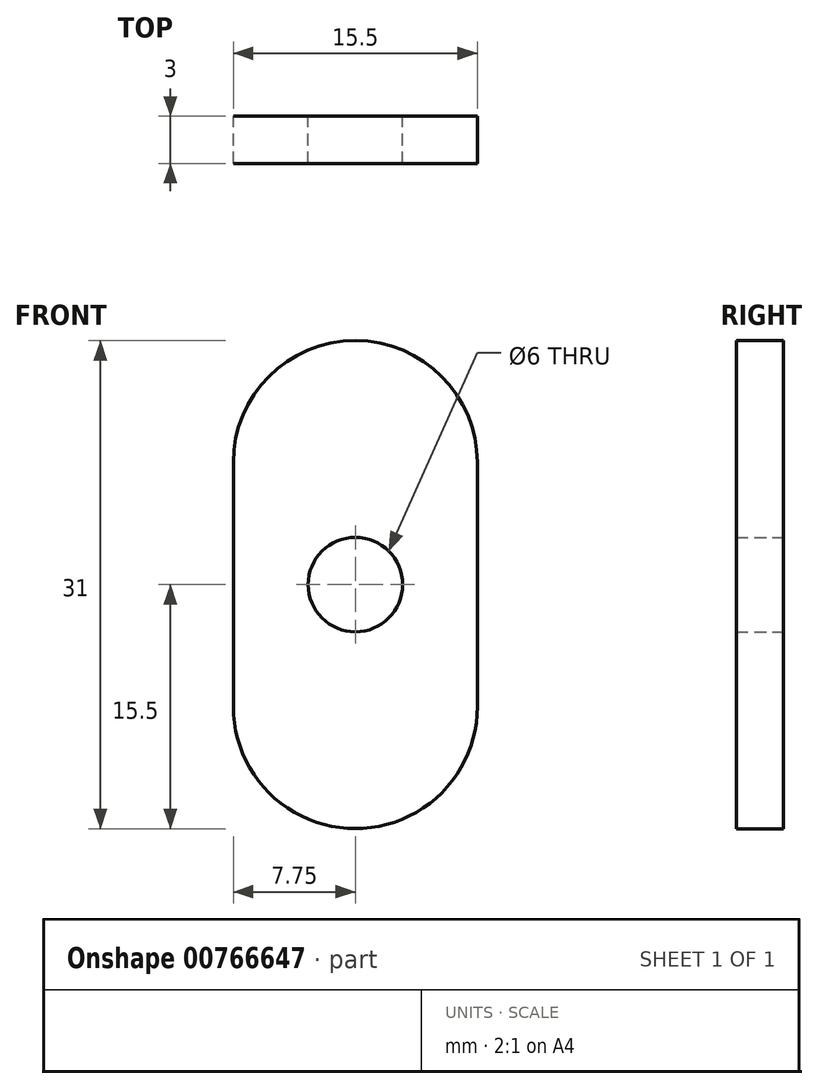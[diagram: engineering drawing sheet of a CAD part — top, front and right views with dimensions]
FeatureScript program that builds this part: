
annotation { "Feature Type Name" : "Feature", "Feature Type Description" : "" }
export const myFeature = defineFeature(function(context is Context, id is Id, definition is map)
    precondition{}
    {
        {
            var Q0;
            Q0=qCreatedBy(makeId("Front.planeOp"),FACE);
            var sketch = newSketch(context, id + "F0", { "sketchPlane" : qUnion([Q0])});
            skLineSegment(sketch, "E0.left", {"start": v(-7.75, -7.75) * mm, "end": v(-7.75, 7.75) * mm});
            skLineSegment(sketch, "E0.right", {"start": v(7.75, -7.75) * mm, "end": v(7.75, 7.75) * mm});
            skPoint(sketch, "E0.middle", {"position": v(0, 0) * mm});
            skArc(sketch, "E1", {"start": v(7.75, 7.75) * mm, "mid": v(0, 15.5) * mm, "end": v(-7.75, 7.75) * mm});
            skArc(sketch, "E2", {"start": v(-7.75, -7.75) * mm, "mid": v(0, -15.5) * mm, "end": v(7.75, -7.75) * mm});
            skCircle(sketch, "E3", {"center": v(0, 0) * mm, "radius": 3 * mm});
            skSolve(sketch);
        }
        {
            var Q0;
            Q0 = qSketchRegion(id + "F0", true);
            extrude(context, id + "F1", {"entities" : qUnion([Q0]), "depth" : 3 * mm, "offsetDistance" : 25 * mm});
        }
    });
